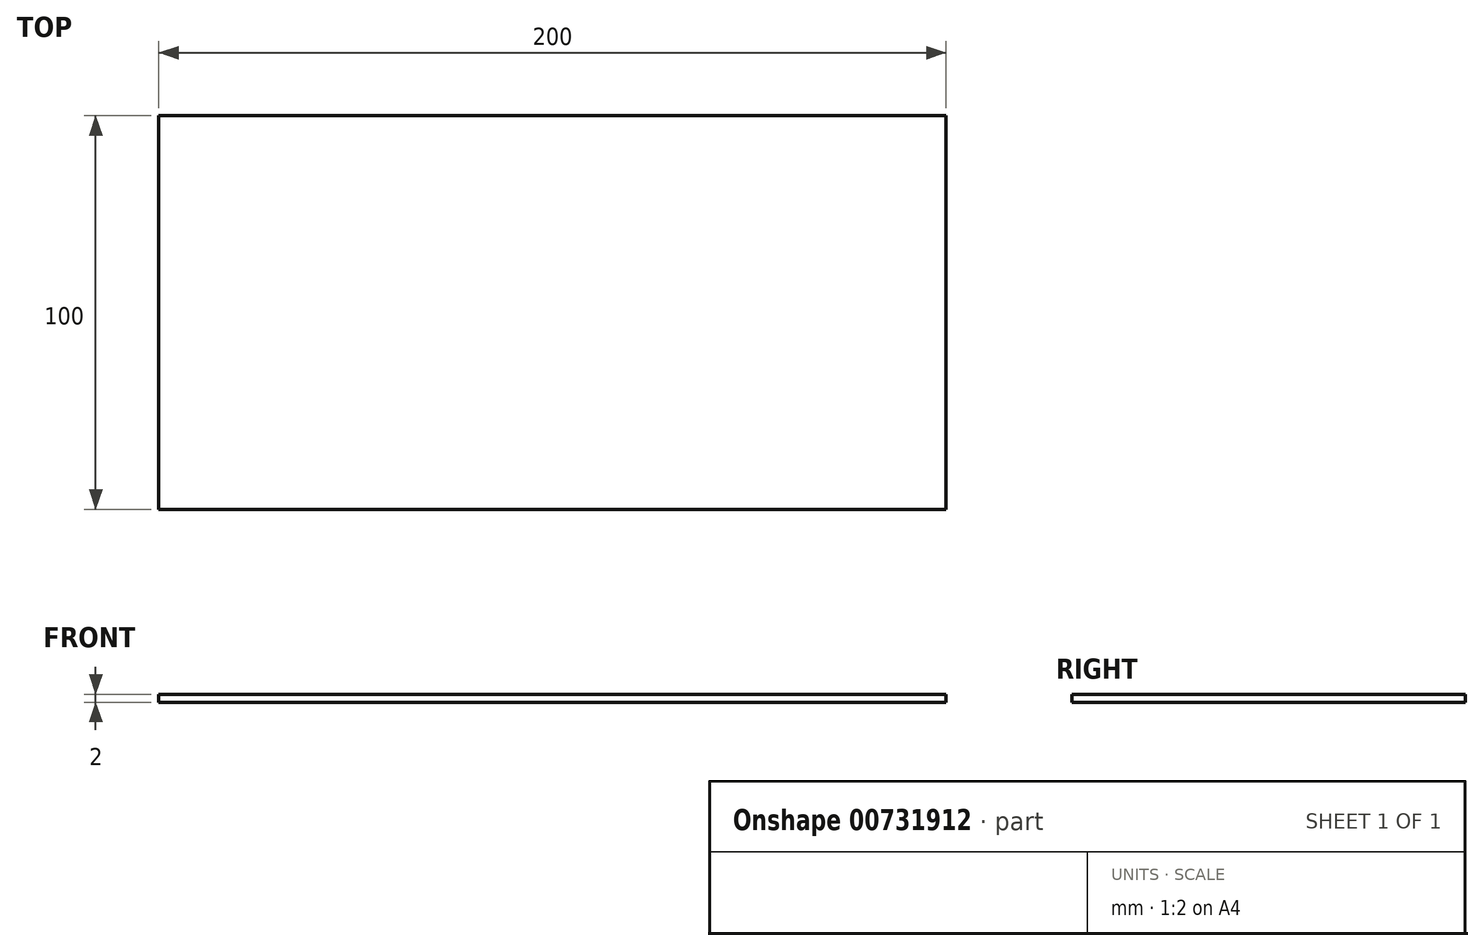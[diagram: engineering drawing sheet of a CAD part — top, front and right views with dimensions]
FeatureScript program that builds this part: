
annotation { "Feature Type Name" : "Feature", "Feature Type Description" : "" }
export const myFeature = defineFeature(function(context is Context, id is Id, definition is map)
    precondition{}
    {
        {
            var Q0;
            Q0=qCreatedBy(makeId("Top.planeOp"),FACE);
            var sketch = newSketch(context, id + "F0", { "sketchPlane" : qUnion([Q0])});
            skLineSegment(sketch, "E0.bottom", {"start": v(100, -50) * mm, "end": v(-100, -50) * mm});
            skLineSegment(sketch, "E0.top", {"start": v(100, 50) * mm, "end": v(-100, 50) * mm});
            skLineSegment(sketch, "E0.left", {"start": v(100, -50) * mm, "end": v(100, 50) * mm});
            skLineSegment(sketch, "E0.right", {"start": v(-100, -50) * mm, "end": v(-100, 50) * mm});
            skPoint(sketch, "E0.middle", {"position": v(0, 0) * mm});
            skSolve(sketch);
        }
        {
            var Q0;
            Q0 = qSketchRegion(id + "F0", true);
            extrude(context, id + "F1", {"entities" : qUnion([Q0]), "depth" : 2 * mm, "offsetDistance" : 25 * mm});
        }
    });
